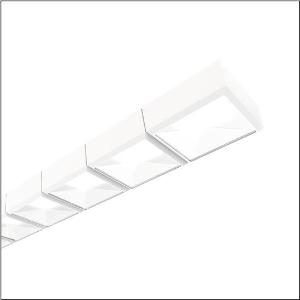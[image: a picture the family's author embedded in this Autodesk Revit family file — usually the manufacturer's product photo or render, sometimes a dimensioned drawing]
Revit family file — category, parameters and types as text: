
# Revit family: scriptus_r__11_5mz223d04wa_758a
name_source: partatom
category: Lighting Fixtures
units: mm (PartAtom-declared; Revit-internal decimal feet)

## family parameters
Cut with Voids When Loaded = No
Host = Face
Light Source = No
Part Type = Normal
Room Calculation Point = No
Round Connector Dimension = Use Diameter
Shared = No

## types (1)
- --- (1 x LED 4000K / CRI = 80 (unbekannt), 7230 lm, 4000K)
    Apparent Load = 51 VA
    CIE Flux Codes = 82 95 99 100 100
    Color Rendering = 80
    Color Temperature = 4000K
    Default Elevation = 1800 mm
    Description = Scriptus® 11, office luminaire, primary optical cover: lenses, CAT 2 (L<= 3000cd/m²), light emission: direct distribution, primary light characteristic: symmetric, installation type: surface-mounted, LED, rated luminous flux: 7.230lm, luminous efficacy: 143lm/W, light colour: 840, colour temperature: 4000K, control gear: ECG DALI, with terminal, 5-pole, mains connection: 230V, AC, 50Hz, rated input power: 51W, housing, luminaire housing, of aluminium, traffic white (RAL 9016), length: 2.426mm, width: 114mm, height: 57mm, protection rating (complete): IP20, insulation class (complete): insulation class I (protective earthing), certification: CE, ENEC, VDE, protection symbol: F, permissible operating ambient temperature: 0..+35°C, standard: EN 50419, packaging unit: 1 piece
    Height = 57 mm
    Lamp = 1 x LED 4000K / CRI >= 80 (unbekannt)
    Lamp Light Flux = 7230 lm
    Lamp count = 1
    Length = 2426 mm
    Luminous efficacy = 143 lm/W
    Manufacturer = Siteco
    ModVariant = No
    Model = 5MZ223D04WA
    Mounting Place = Ceiling
    Mounting Type = Surface mounted
    Number of Poles = 1
    OnlyDefault = Yes
    Power Factor = 1
    Product Name = Scriptus® 11
    Product group = office luminaire | ceiling mounted
    ProductGroupID = 304
    Protection Class = Protection class I
    Protection Degree = IP 20
    RLX_Detail_Level = 1
    RLX_Emergency_Light_Flux = 0 lm
    RLX_Emergency_Type = 0
    RLX_Emergency_Type_DB = No
    RlxData = <blob elided: 31377 chars, md5=74055da9>
    Socket = socket
    Standby Power = 0 W
    System Light Flux = 7230 lm
    System Power = 51 W
    Type Comments = factory setting: luminous flux: 100 % | dim-lin: 254 | 525 mA
    Type Image = l_1004833.jpg
    URL = http://relux.com
    VarID = @adj_179649
    Voltage = 0 V
    Weight = 0.00 kg
    Width = 114 mm

## geometry (parser evidence)
native form markers: Blend x4, Sweep x9
no freeform markers — native parametric forms only
